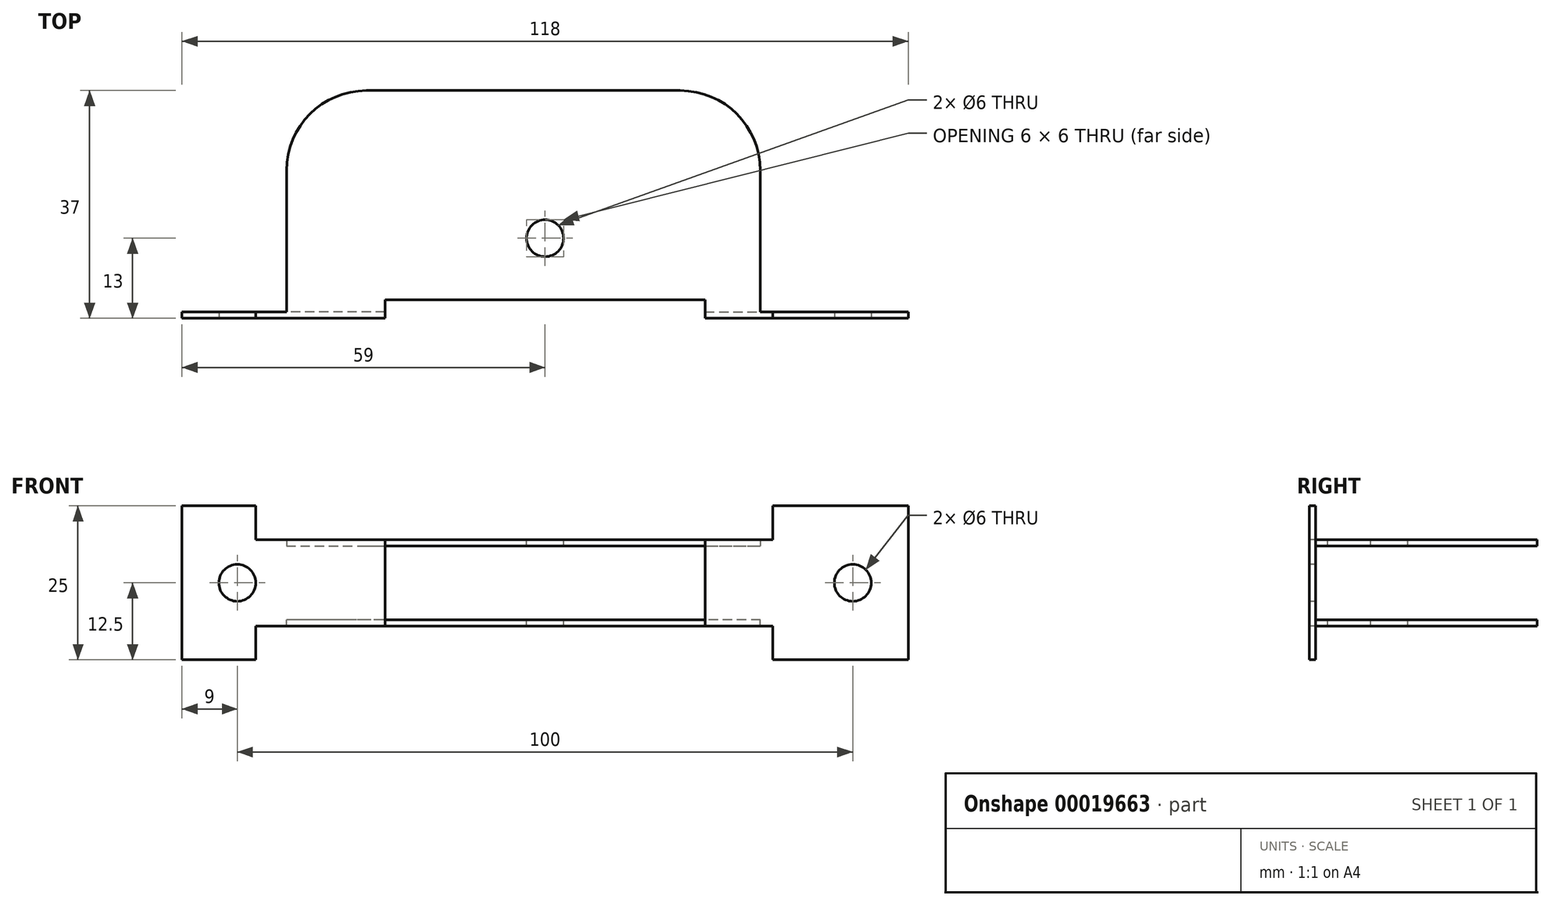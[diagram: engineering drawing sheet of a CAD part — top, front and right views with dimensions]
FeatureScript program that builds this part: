
annotation { "Feature Type Name" : "Feature", "Feature Type Description" : "" }
export const myFeature = defineFeature(function(context is Context, id is Id, definition is map)
    precondition{}
    {
        {
            var Q0;
            Q0=qCreatedBy(makeId("Front.planeOp"),FACE);
            var sketch = newSketch(context, id + "F0", { "sketchPlane" : qUnion([Q0])});
            skLineSegment(sketch, "E0.rect.bottom", {"start": v(-59, 12.5) * mm, "end": v(59, 12.5) * mm});
            skLineSegment(sketch, "E0.rect.top", {"start": v(-59, -12.5) * mm, "end": v(59, -12.5) * mm});
            skLineSegment(sketch, "E0.rect.left", {"start": v(-59, 12.5) * mm, "end": v(-59, -12.5) * mm});
            skLineSegment(sketch, "E0.rect.right", {"start": v(59, 12.5) * mm, "end": v(59, -12.5) * mm});
            skPoint(sketch, "E0.rect.middle", {"position": v(0, 0) * mm});
            skLineSegment(sketch, "E1.bottom", {"start": v(-47, 12.5) * mm, "end": v(37, 12.5) * mm});
            skLineSegment(sketch, "E1.top", {"start": v(-47, 7) * mm, "end": v(37, 7) * mm});
            skLineSegment(sketch, "E1.left", {"start": v(-47, 12.5) * mm, "end": v(-47, 7) * mm});
            skLineSegment(sketch, "E1.right", {"start": v(37, 12.5) * mm, "end": v(37, 7) * mm});
            skLineSegment(sketch, "E2.bottom", {"start": v(-47, -12.5) * mm, "end": v(37, -12.5) * mm});
            skLineSegment(sketch, "E2.top", {"start": v(-47, -7) * mm, "end": v(37, -7) * mm});
            skLineSegment(sketch, "E2.left", {"start": v(-47, -12.5) * mm, "end": v(-47, -7) * mm});
            skLineSegment(sketch, "E2.right", {"start": v(37, -12.5) * mm, "end": v(37, -7) * mm});
            skCircle(sketch, "E3", {"center": v(-50, 0) * mm, "radius": 3 * mm});
            skCircle(sketch, "E4", {"center": v(50, 0) * mm, "radius": 3 * mm});
            skSolve(sketch);
        }
        {
            var Q0;
            {var subQ4=sQuery(id+"F0.wireOp",EDGE,"E0.rect.left");Q0=makeQuery(id+"F0.imprint","IMPRINT",FACE,{"disambiguationData":[TD([[makeQuery(id+"F0.imprint","IMPRINT",EDGE,{"derivedFrom":subQ4}),1.0]])]});}
            extrude(context, id + "F1", {"entities" : qUnion([Q0]), "oppositeDirection" : true, "depth" : 1 * mm});
        }
        {
            var Q0;
            Q0=qCreatedBy(makeId("Front.planeOp"),FACE);
            var sketch = newSketch(context, id + "F2", { "sketchPlane" : qUnion([Q0])});
            skLineSegment(sketch, "E5.bottom", {"start": v(-42.02, 7) * mm, "end": v(34.98, 7) * mm});
            skLineSegment(sketch, "E5.top", {"start": v(-42.02, 6) * mm, "end": v(34.98, 6) * mm});
            skLineSegment(sketch, "E5.left", {"start": v(-42.02, 7) * mm, "end": v(-42.02, 6) * mm});
            skLineSegment(sketch, "E5.right", {"start": v(34.98, 7) * mm, "end": v(34.98, 6) * mm});
            skLineSegment(sketch, "E6.bottom", {"start": v(34.98, -7) * mm, "end": v(-42.02, -7) * mm});
            skLineSegment(sketch, "E6.top", {"start": v(34.98, -6) * mm, "end": v(-42.02, -6) * mm});
            skLineSegment(sketch, "E6.left", {"start": v(34.98, -7) * mm, "end": v(34.98, -6) * mm});
            skLineSegment(sketch, "E6.right", {"start": v(-42.02, -7) * mm, "end": v(-42.02, -6) * mm});
            skSolve(sketch);
        }
        {
            var Q0;
            Q0 = qSketchRegion(id + "F2", true);
            var Q1;
            Q1 = qSketchRegion(id + "FOr8h0gMZWFF12a_1", true);
            extrude(context, id + "F3", {"entities" : qUnion([Q0, Q1]), "operationType" : NewBodyOperationType.ADD, "oppositeDirection" : true, "depth" : 37 * mm});
        }
        {
            var Q0;
            Q0=makeQuery(id+"F1.opExtrude","CAP_FACE",FACE,{"disambiguationData":[OSD([sQuery(id+"F0.wireOp",EDGE,"E0.rect.bottom"),sQuery(id+"F0.wireOp",EDGE,"E0.rect.top"),sQuery(id+"F0.wireOp",EDGE,"E0.rect.left"),sQuery(id+"F0.wireOp",EDGE,"E0.rect.right"),sQuery(id+"F0.wireOp",EDGE,"E1.top"),sQuery(id+"F0.wireOp",EDGE,"E1.left"),sQuery(id+"F0.wireOp",EDGE,"E1.right"),sQuery(id+"F0.wireOp",EDGE,"E2.top"),sQuery(id+"F0.wireOp",EDGE,"E2.left"),sQuery(id+"F0.wireOp",EDGE,"E2.right"),sQuery(id+"F0.wireOp",EDGE,"E3"),sQuery(id+"F0.wireOp",EDGE,"E4")])],"isStart":true});
            var sketch = newSketch(context, id + "F4", { "sketchPlane" : qUnion([Q0])});
            skLineSegment(sketch, "E7.rect.bottom", {"start": v(26, -7.5) * mm, "end": v(-26, -7.5) * mm});
            skLineSegment(sketch, "E7.rect.top", {"start": v(26, 7.5) * mm, "end": v(-26, 7.5) * mm});
            skLineSegment(sketch, "E7.rect.left", {"start": v(26, -7.5) * mm, "end": v(26, 7.5) * mm});
            skLineSegment(sketch, "E7.rect.right", {"start": v(-26, -7.5) * mm, "end": v(-26, 7.5) * mm});
            skPoint(sketch, "E7.rect.middle", {"position": v(0, 0) * mm});
            skSolve(sketch);
        }
        {
            var Q0;
            Q0=makeQuery(id+"F3.boolean.opBoolean","MERGE",FACE,{"derivedFrom":[makeQuery(id+"F1.opExtrude","SWEPT_FACE",FACE,{"disambiguationData":[OSD([sQuery(id+"F0.wireOp",EDGE,"E1.top")])]}),makeQuery(id+"F3.opExtrude","SWEPT_FACE",FACE,{"disambiguationData":[OSD([sQuery(id+"F2.wireOp",EDGE,"E5.bottom")])]})]});
            var sketch = newSketch(context, id + "F5", { "sketchPlane" : qUnion([Q0])});
            skLineSegment(sketch, "E8", {"start": v(-42.02, 37) * mm, "end": v(-29.02, 24) * mm});
            skCircle(sketch, "E9", {"center": v(-29.02, 24) * mm, "radius": 13 * mm});
            skSolve(sketch);
        }
        {
            var Q0;
            {var subQ2=sQuery(id+"F5.wireOp",EDGE,"E9");var subQ4=sQuery(id+"F5.wireOp",EDGE,"E8");var subQ6=makeQuery(id+"F5.imprint","INTERSECT",VERTEX,{"derivedFrom":[subQ4,subQ2]});Q0=makeQuery(id+"F5.imprint","IMPRINT",FACE,{"disambiguationData":[TD([[makeQuery(id+"F5.imprint","IMPRINT",EDGE,{"disambiguationData":[TD([[subQ6,-1.0]])],"derivedFrom":subQ2}),-1.0]])]});}
            var Q1;
            {var subQ2=sQuery(id+"F5.wireOp",EDGE,"E9");var subQ4=sQuery(id+"F5.wireOp",EDGE,"E8");var subQ6=makeQuery(id+"F5.imprint","INTERSECT",VERTEX,{"derivedFrom":[subQ4,subQ2]});Q1=makeQuery(id+"F5.imprint","IMPRINT",FACE,{"disambiguationData":[TD([[makeQuery(id+"F5.imprint","IMPRINT",EDGE,{"disambiguationData":[TD([[subQ6,1.0]])],"derivedFrom":subQ2}),-1.0]])]});}
            extrude(context, id + "F6", {"entities" : qUnion([Q0, Q1]), "operationType" : NewBodyOperationType.REMOVE, "endBound" : BoundingType.THROUGH_ALL, "oppositeDirection" : true, "depth" : 25 * mm, "hasSecondDirection" : true, "secondDirectionOppositeDirection" : false, "secondDirectionDepth" : 25 * mm});
        }
        {
            var Q0;
            Q0=makeQuery(id+"F3.boolean.opBoolean","MERGE",FACE,{"derivedFrom":[makeQuery(id+"F1.opExtrude","SWEPT_FACE",FACE,{"disambiguationData":[OSD([sQuery(id+"F0.wireOp",EDGE,"E1.top")])]}),makeQuery(id+"F3.opExtrude","SWEPT_FACE",FACE,{"disambiguationData":[OSD([sQuery(id+"F2.wireOp",EDGE,"E5.bottom")])]})]});
            var sketch = newSketch(context, id + "F7", { "sketchPlane" : qUnion([Q0])});
            skLineSegment(sketch, "E10", {"start": v(34.98, 37) * mm, "end": v(21.98, 24) * mm});
            skCircle(sketch, "E11", {"center": v(21.98, 24) * mm, "radius": 13 * mm});
            skSolve(sketch);
        }
        {
            var Q0;
            {var subQ2=sQuery(id+"F7.wireOp",EDGE,"E11");var subQ4=sQuery(id+"F7.wireOp",EDGE,"E10");var subQ6=makeQuery(id+"F7.imprint","INTERSECT",VERTEX,{"derivedFrom":[subQ4,subQ2]});Q0=makeQuery(id+"F7.imprint","IMPRINT",FACE,{"disambiguationData":[TD([[makeQuery(id+"F7.imprint","IMPRINT",EDGE,{"disambiguationData":[TD([[subQ6,-1.0]])],"derivedFrom":subQ2}),-1.0]])]});}
            var Q1;
            {var subQ2=sQuery(id+"F7.wireOp",EDGE,"E11");var subQ4=sQuery(id+"F7.wireOp",EDGE,"E10");var subQ6=makeQuery(id+"F7.imprint","INTERSECT",VERTEX,{"derivedFrom":[subQ4,subQ2]});Q1=makeQuery(id+"F7.imprint","IMPRINT",FACE,{"disambiguationData":[TD([[makeQuery(id+"F7.imprint","IMPRINT",EDGE,{"disambiguationData":[TD([[subQ6,1.0]])],"derivedFrom":subQ2}),-1.0]])]});}
            extrude(context, id + "F8", {"entities" : qUnion([Q0, Q1]), "operationType" : NewBodyOperationType.REMOVE, "oppositeDirection" : true, "depth" : 25 * mm});
        }
        {
            var Q0;
            {var subQ0=makeQuery(id+"F1.opExtrude","CAP_EDGE",EDGE,{"disambiguationData":[OSD([sQuery(id+"F0.wireOp",EDGE,"E2.top")])],"isStart":true});var subQ3=sQuery(id+"F4.wireOp",EDGE,"E7.rect.left");var subQ4=makeQuery(id+"F4.imprint","INTERSECT",VERTEX,{"derivedFrom":[subQ0,subQ3]});Q0=makeQuery(id+"F4.imprint","IMPRINT",FACE,{"disambiguationData":[TD([[makeQuery(id+"F4.imprint","IMPRINT",EDGE,{"disambiguationData":[TD([[subQ4,-1.0]])],"derivedFrom":subQ3}),1.0]])]});}
            extrude(context, id + "F9", {"entities" : qUnion([Q0]), "operationType" : NewBodyOperationType.REMOVE, "oppositeDirection" : true, "depth" : 3 * mm});
        }
        {
            var Q0;
            Q0=makeQuery(id+"F3.boolean.opBoolean","MERGE",FACE,{"derivedFrom":[makeQuery(id+"F1.opExtrude","SWEPT_FACE",FACE,{"disambiguationData":[OSD([sQuery(id+"F0.wireOp",EDGE,"E1.top")])]}),makeQuery(id+"F3.opExtrude","SWEPT_FACE",FACE,{"disambiguationData":[OSD([sQuery(id+"F2.wireOp",EDGE,"E5.bottom")])]})]});
            var sketch = newSketch(context, id + "F10", { "sketchPlane" : qUnion([Q0])});
            skCircle(sketch, "E12", {"center": v(0, 13) * mm, "radius": 3 * mm});
            skSolve(sketch);
        }
        {
            var Q0;
            Q0=makeQuery(id+"F10.imprint","IMPRINT",FACE,{"disambiguationData":[TD([[makeQuery(id+"F10.imprint","IMPRINT",EDGE,{"derivedFrom":sQuery(id+"F10.wireOp",EDGE,"E12")}),1.0]])]});
            extrude(context, id + "F11", {"entities" : qUnion([Q0]), "operationType" : NewBodyOperationType.REMOVE, "oppositeDirection" : true, "depth" : 25 * mm});
        }
    });
